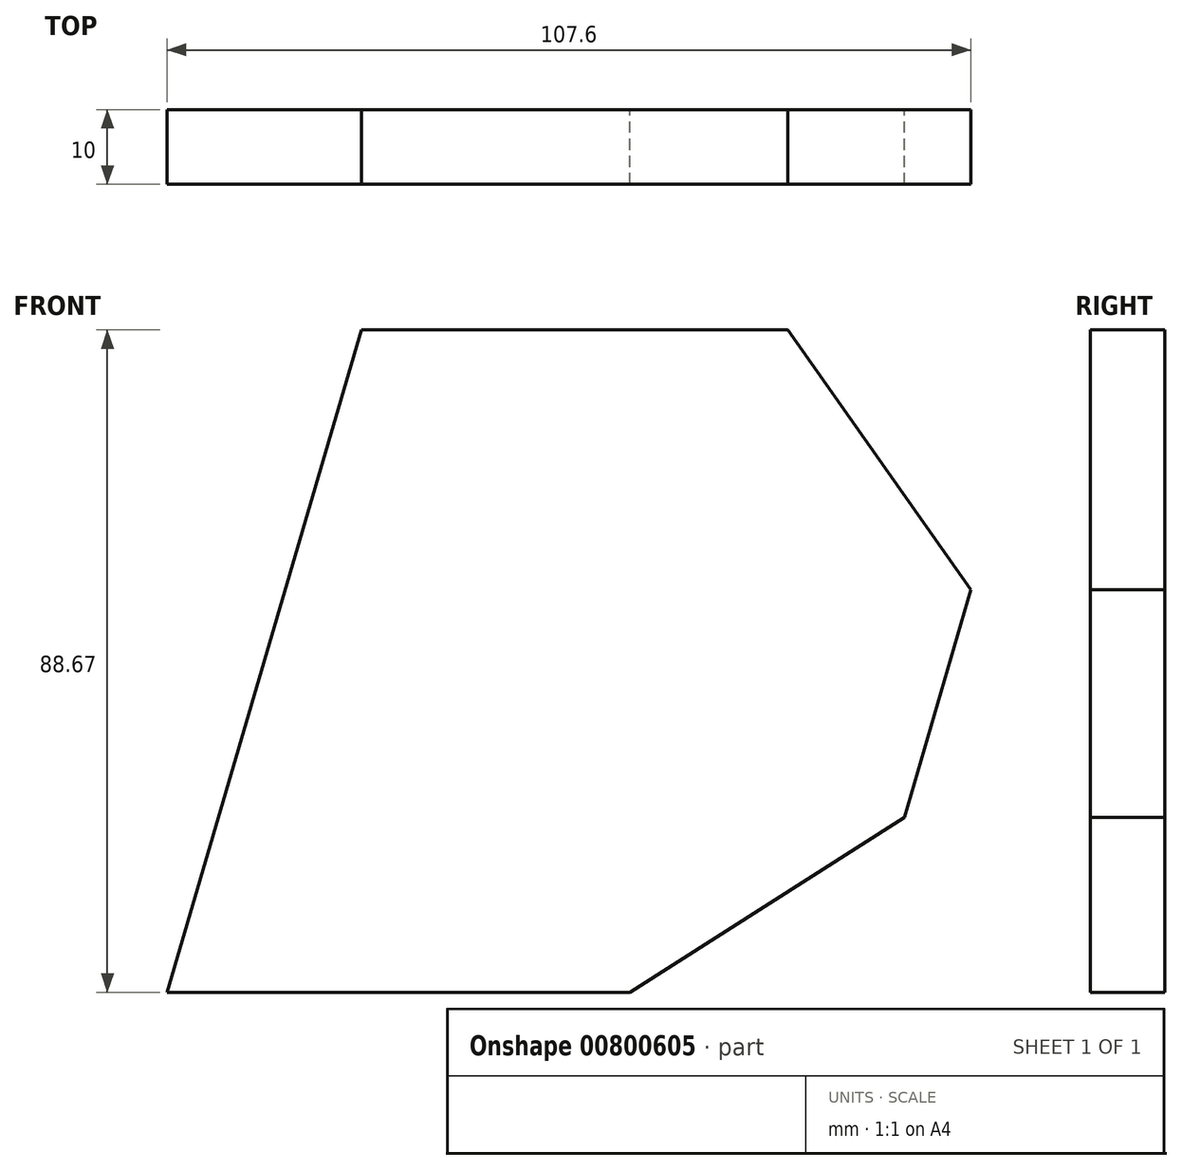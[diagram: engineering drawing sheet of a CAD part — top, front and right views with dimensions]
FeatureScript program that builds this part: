
annotation { "Feature Type Name" : "Feature", "Feature Type Description" : "" }
export const myFeature = defineFeature(function(context is Context, id is Id, definition is map)
    precondition{}
    {
        {
            var Q0;
            Q0=qCreatedBy(makeId("Front.planeOp"),FACE);
            var sketch = newSketch(context, id + "F0", { "sketchPlane" : qUnion([Q0])});
            skLineSegment(sketch, "E0", {"start": v(0, 0) * mm, "end": v(61.94, 0) * mm});
            skLineSegment(sketch, "E1", {"start": v(61.94, 0) * mm, "end": v(98.72, 23.42) * mm});
            skLineSegment(sketch, "E2", {"start": v(98.72, 23.42) * mm, "end": v(107.6, 53.9) * mm});
            skLineSegment(sketch, "E3", {"start": v(107.6, 53.9) * mm, "end": v(83.08, 88.67) * mm});
            skLineSegment(sketch, "E4", {"start": v(83.08, 88.67) * mm, "end": v(26, 88.67) * mm});
            skLineSegment(sketch, "E5", {"start": v(26, 88.67) * mm, "end": v(0, 0) * mm});
            skSolve(sketch);
        }
        {
            var Q0;
            Q0 = qSketchRegion(id + "F0", true);
            extrude(context, id + "F1", {"entities" : qUnion([Q0]), "depth" : 10 * mm, "offsetDistance" : 25.4 * mm});
        }
    });
